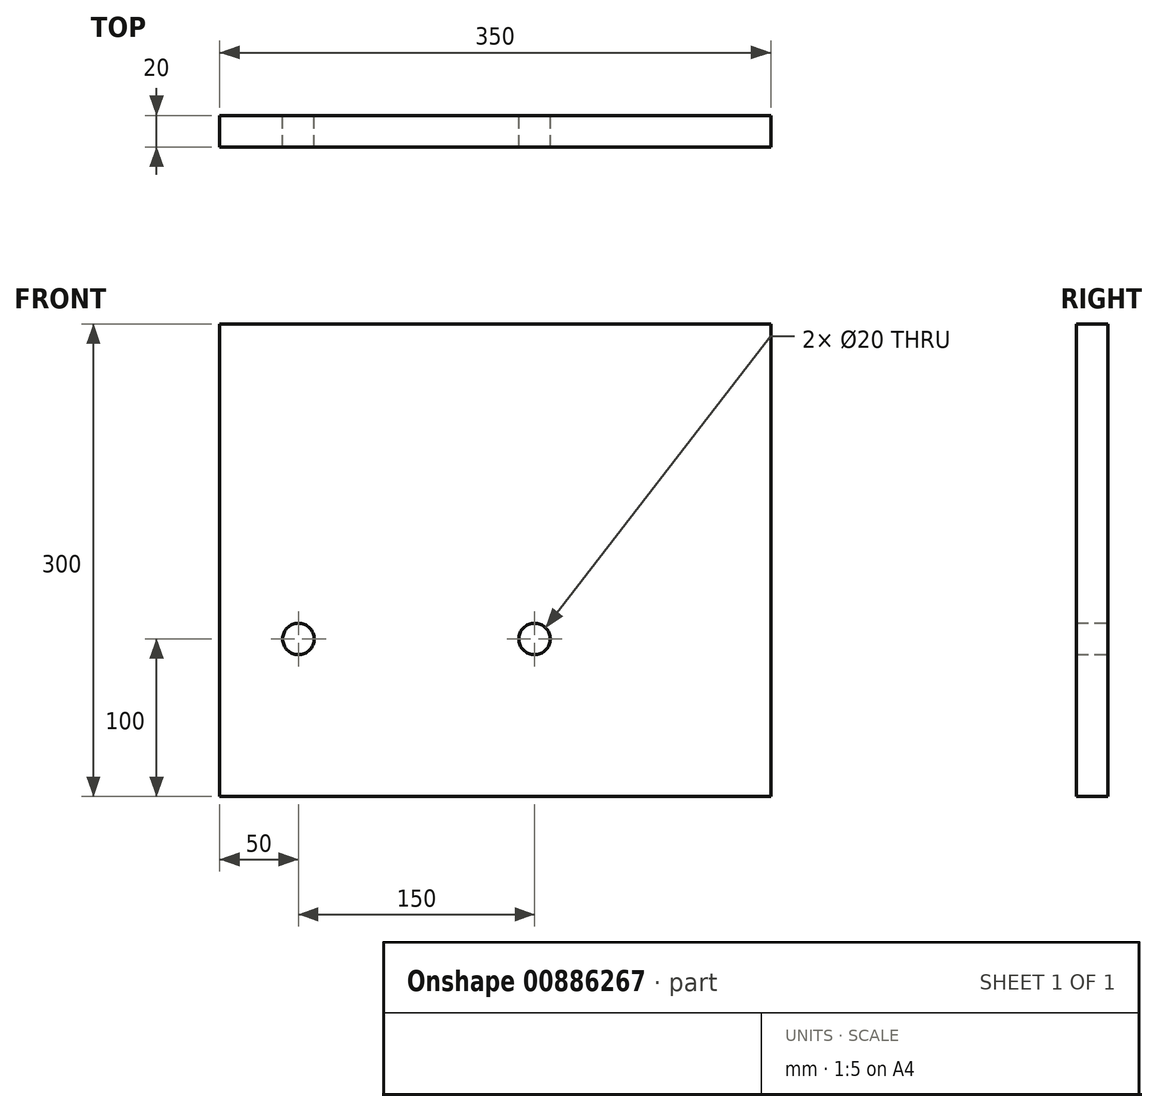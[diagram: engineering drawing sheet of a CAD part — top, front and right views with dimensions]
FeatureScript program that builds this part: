
annotation { "Feature Type Name" : "Feature", "Feature Type Description" : "" }
export const myFeature = defineFeature(function(context is Context, id is Id, definition is map)
    precondition{}
    {
        {
            var Q0;
            Q0=qCreatedBy(makeId("Front.planeOp"),FACE);
            var sketch = newSketch(context, id + "F0", { "sketchPlane" : qUnion([Q0])});
            skLineSegment(sketch, "E0.bottom", {"start": v(-175, 150) * mm, "end": v(175, 150) * mm});
            skLineSegment(sketch, "E0.top", {"start": v(-175, -150) * mm, "end": v(175, -150) * mm});
            skLineSegment(sketch, "E0.left", {"start": v(-175, 150) * mm, "end": v(-175, -150) * mm});
            skLineSegment(sketch, "E0.right", {"start": v(175, 150) * mm, "end": v(175, -150) * mm});
            skPoint(sketch, "E0.middle", {"position": v(0, 0) * mm});
            skCircle(sketch, "E1", {"center": v(-125, -50) * mm, "radius": 10 * mm});
            skCircle(sketch, "E2", {"center": v(25, -50) * mm, "radius": 10 * mm});
            skSolve(sketch);
        }
        {
            var Q0;
            Q0 = qSketchRegion(id + "F0", true);
            extrude(context, id + "F1", {"entities" : qUnion([Q0]), "depth" : 20 * mm, "offsetDistance" : 25 * mm, "symmetric" : true});
        }
    });
